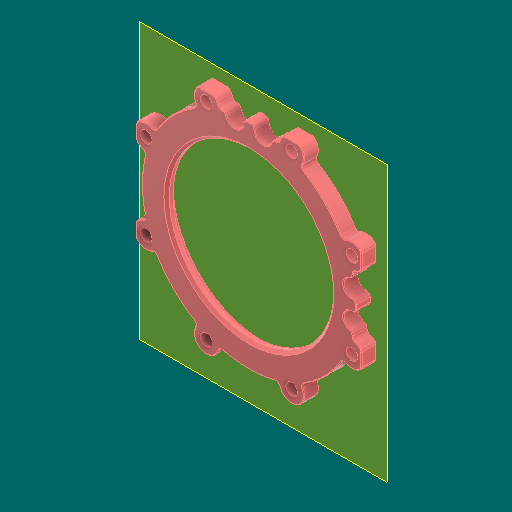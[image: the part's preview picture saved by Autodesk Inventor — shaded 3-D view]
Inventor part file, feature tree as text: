
AUTODESK INVENTOR PART (.ipt)
format: ipt  version: 2023.1 (Build 271208000, 208)  size: 843,776 bytes
history: native  units: in
note: dims shown in document units (in); Inventor stores cm internally (conversion verified against a paired STEP export)
features: chamfer x5, other x4, reference x3, fillet x2, plane x1, revolve x1, extrude x1, sketch x1
ambient origin geometry x8: Origin, YZ Plane, XZ Plane, XY Plane, X Axis, Y Axis, Z Axis, Center Point
bodies: Solid1 (feature_tree)
feature tree (18):
  plane  "Work Plane1"
  revolve  "Revolution1"  [1 undecoded]
  extrude  "Extrusion1"  Depth=0.0625in
  fillet  "Fillet2"  Radius=0.125in
  chamfer  "Chamfer2"  Angle=360.0deg  [1 undecoded]
  chamfer  "Chamfer3"  Distance=0.25in
  chamfer  "Chamfer4"  Distance=0.25in
  fillet  "Fillet3"  Radius=0.0472in
  chamfer  "Chamfer5"  Distance=0.3in
  chamfer  "Chamfer1"  Distance=0.3in
  reference  "Reference1"
  sketch  "Sketch2"  dims[d0=0.19in d5=0.25in d7=0.4331in d8=0.125in d18=360.0deg d19=0.25in d20=0.0in d21=0.25in d23=0.0472in d24=0.125in d25=45.0deg d26=0.3in d27=0.3in d32=0.0625in d33=0.2756in d34=3.1437in d35=0.125in d36=3.25in d37=0.0472in d38=0.125in d39=45.0deg d40=0.0118in d41=0.125in d42=45.0deg d43=0.0118in d44=0.125in d45=45.0deg d46=0.0625in d47=0.0118in d48=0.125in d49=45.0deg]
  reference  "Reference2"
  reference  "Reference4"
  other  "<userpath>\Documents\CAD\guardSwerve5\MainAssy.iam"
  other  "MainAssy.iam"
  other  "Baseplate:1"
  other  "608bearing:1"
note: 2 required parameter values undecoded (feature->parameter linkage not recoverable at this tier; creation-order binding heuristic only, values carry confidence <= 0.55)